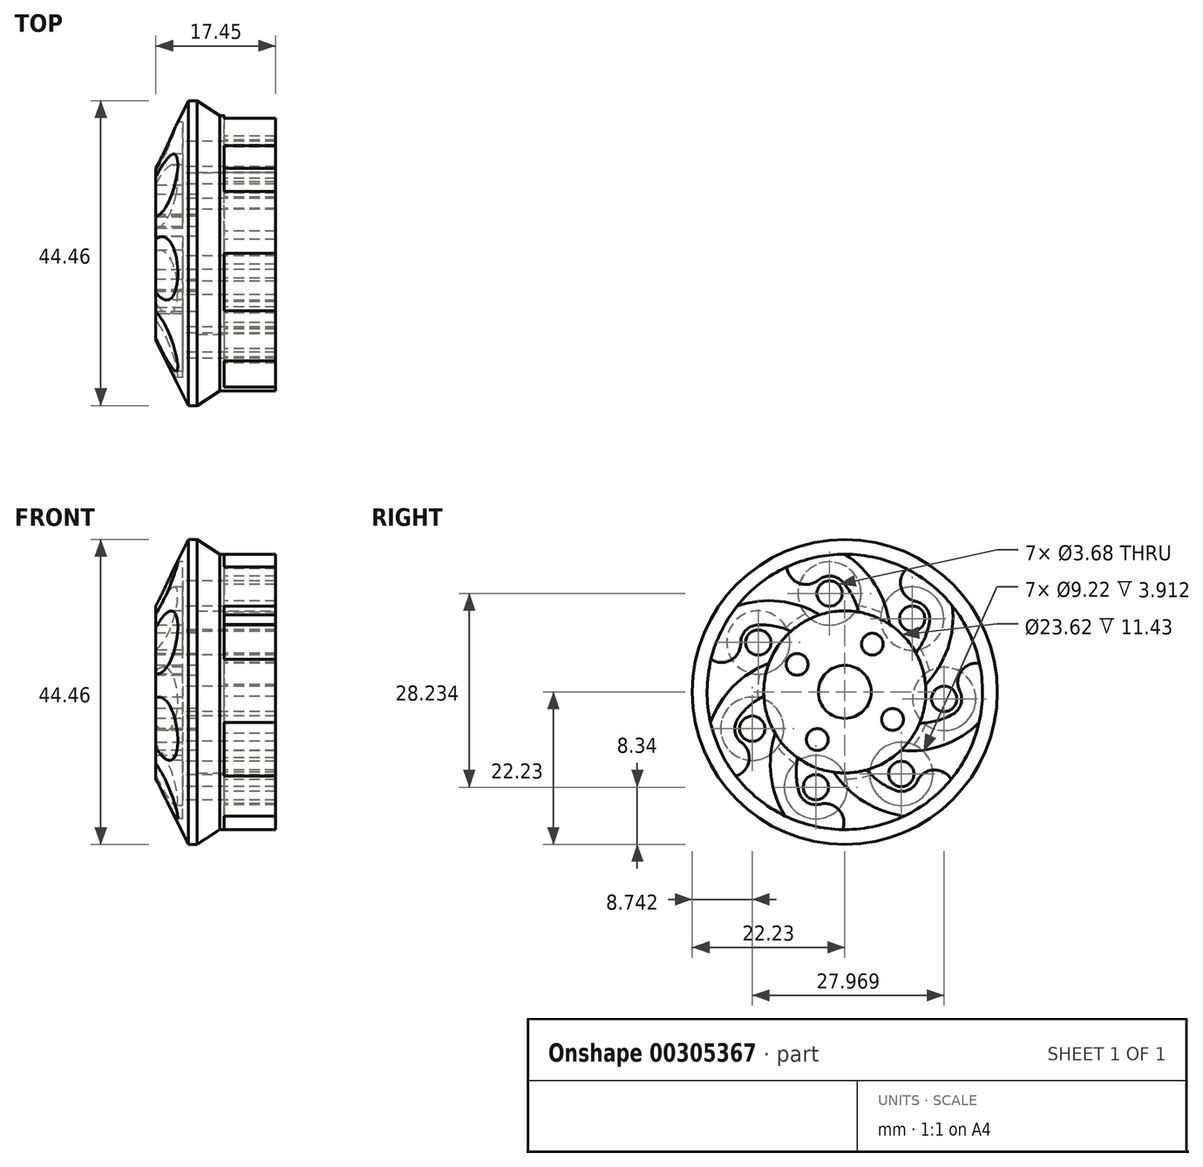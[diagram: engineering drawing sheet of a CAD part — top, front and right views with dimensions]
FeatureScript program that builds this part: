
annotation { "Feature Type Name" : "Feature", "Feature Type Description" : "" }
export const myFeature = defineFeature(function(context is Context, id is Id, definition is map)
    precondition{}
    {
        {
            var Q0;
            Q0=qCreatedBy(makeId("Top.planeOp"),FACE);
            var sketch = newSketch(context, id + "F0", { "sketchPlane" : qUnion([Q0])});
            skLineSegment(sketch, "E0", {"start": v(17.45, 0) * mm, "end": v(17.45, -12.7) * mm});
            skLineSegment(sketch, "E1", {"start": v(17.45, -12.7) * mm, "end": v(12.7, -22.23) * mm});
            skLineSegment(sketch, "E2", {"start": v(12.7, -22.23) * mm, "end": v(11.43, -22.23) * mm});
            skLineSegment(sketch, "E3", {"start": v(11.43, -22.23) * mm, "end": v(8.13, -20.07) * mm});
            skLineSegment(sketch, "E4", {"start": v(8.13, -20.07) * mm, "end": v(0, -20.07) * mm});
            skLineSegment(sketch, "E5", {"start": v(0, -20.07) * mm, "end": v(0, -11.81) * mm});
            skLineSegment(sketch, "E6", {"start": v(0, -11.81) * mm, "end": v(11.43, -11.81) * mm});
            skLineSegment(sketch, "E7", {"start": v(11.43, -11.81) * mm, "end": v(11.43, 0) * mm});
            skLineSegment(sketch, "E8", {"start": v(11.43, 0) * mm, "end": v(17.45, 0) * mm});
            skLineSegment(sketch, "E9", {"start": v(40.63, 0) * mm, "end": v(0, 0) * mm, "construction": true});
            skSolve(sketch);
        }
        {
            var Q0;
            Q0=qSketchRegion(id+"F0",true);
            var Q1;
            Q1=sQuery(id+"F0.wireOp",EDGE,"E9");
            revolve(context, id + "F1", {"entities" : qUnion([Q0]), "axis" : qUnion([Q1]), "revolveType" : RevolveType.FULL});
        }
        {
            var Q0;
            Q0=qCreatedBy(makeId("Right.planeOp"),FACE);
            var sketch = newSketch(context, id + "F2", { "sketchPlane" : qUnion([Q0])});
            skCircle(sketch, "E10.cCircle", {"center": v(0, 0) * mm, "radius": 20.07 * mm, "construction": true});
            skLineSegment(sketch, "E10.0", {"start": v(-9.66, 20.07) * mm, "end": v(9.66, 20.07) * mm, "construction": true});
            skLineSegment(sketch, "E10.1", {"start": v(9.66, 20.07) * mm, "end": v(21.71, 4.96) * mm, "construction": true});
            skLineSegment(sketch, "E10.2", {"start": v(21.71, 4.96) * mm, "end": v(17.41, -13.89) * mm, "construction": true});
            skLineSegment(sketch, "E10.3", {"start": v(17.41, -13.89) * mm, "end": v(0, -22.27) * mm, "construction": true});
            skLineSegment(sketch, "E10.4", {"start": v(0, -22.27) * mm, "end": v(-17.41, -13.89) * mm, "construction": true});
            skLineSegment(sketch, "E10.5", {"start": v(-17.41, -13.89) * mm, "end": v(-21.71, 4.96) * mm, "construction": true});
            skLineSegment(sketch, "E10.6", {"start": v(-21.71, 4.96) * mm, "end": v(-9.66, 20.07) * mm, "construction": true});
            skPoint(sketch, "E10.0.midPoint", {"position": v(0, 20.07) * mm});
            skLineSegment(sketch, "E11", {"start": v(0, 0) * mm, "end": v(0, 20.07) * mm, "construction": true});
            skLineSegment(sketch, "E12", {"start": v(0, 0) * mm, "end": v(-8.43, 18.2) * mm, "construction": true});
            skLineSegment(sketch, "E13", {"start": v(0, 0) * mm, "end": v(2.02, 11.64) * mm, "construction": true});
            skCircle(sketch, "E14", {"center": v(0, 0) * mm, "radius": 11.81 * mm, "construction": true});
            skPoint(sketch, "E15", {"position": v(0, 11.81) * mm});
            skLineSegment(sketch, "E16", {"start": v(0, 0) * mm, "end": v(6.5, 9.86) * mm, "construction": true});
            skArc(sketch, "E17", {"start": v(6.5, 9.86) * mm, "mid": v(4.4, 15.68) * mm, "end": v(0, 20.07) * mm});
            skCircle(sketch, "E18", {"center": v(0, 0) * mm, "radius": 14.52 * mm, "construction": true});
            skLineSegment(sketch, "E19", {"start": v(0, 0) * mm, "end": v(-2.23, 14.34) * mm, "construction": true});
            skPoint(sketch, "E20", {"position": v(0, 14.52) * mm});
            skCircle(sketch, "E21", {"center": v(-2.23, 14.34) * mm, "radius": 1.84 * mm, "construction": true});
            skArc(sketch, "E22", {"start": v(-0.35, 16.07) * mm, "mid": v(-2.06, 16.9) * mm, "end": v(-3.86, 16.3) * mm});
            skArc(sketch, "E23", {"start": v(2.02, 11.64) * mm, "mid": v(1.12, 14) * mm, "end": v(-0.35, 16.07) * mm});
            skArc(sketch, "E24", {"start": v(-8.43, 18.2) * mm, "mid": v(-6.72, 15.87) * mm, "end": v(-3.86, 16.3) * mm});
            skArc(sketch, "E25", {"start": v(0, 20.07) * mm, "mid": v(-4.73, 21.48) * mm, "end": v(-8.43, 18.2) * mm});
            skArc(sketch, "E26", {"start": v(2.02, 11.64) * mm, "mid": v(4.04, 10.18) * mm, "end": v(6.5, 9.86) * mm});
            skCircle(sketch, "E27", {"center": v(-2.23, 14.34) * mm, "radius": 1.84 * mm});
            skArc(sketch, "E28.1.0", {"start": v(-3.65, 11.23) * mm, "mid": v(-9.53, 13.21) * mm, "end": v(-15.69, 12.51) * mm});
            skArc(sketch, "E28.1.1", {"start": v(-7.84, 8.84) * mm, "mid": v(-5.44, 9.5) * mm, "end": v(-3.65, 11.23) * mm});
            skArc(sketch, "E28.1.2", {"start": v(-7.84, 8.84) * mm, "mid": v(-10.25, 9.6) * mm, "end": v(-12.78, 9.75) * mm});
            skArc(sketch, "E28.1.3", {"start": v(-12.78, 9.75) * mm, "mid": v(-14.49, 8.92) * mm, "end": v(-15.16, 7.15) * mm});
            skArc(sketch, "E28.1.4", {"start": v(-15.69, 12.51) * mm, "mid": v(-19.75, 9.7) * mm, "end": v(-19.5, 4.76) * mm});
            skArc(sketch, "E28.1.5", {"start": v(-19.5, 4.76) * mm, "mid": v(-16.6, 4.64) * mm, "end": v(-15.16, 7.15) * mm});
            skCircle(sketch, "E28.1.6", {"center": v(-12.6, 7.2) * mm, "radius": 1.84 * mm, "construction": true});
            skCircle(sketch, "E28.1.7", {"center": v(-12.6, 7.2) * mm, "radius": 1.84 * mm});
            skArc(sketch, "E28.2.0", {"start": v(-11.06, 4.15) * mm, "mid": v(-16.27, 0.8) * mm, "end": v(-19.56, -4.47) * mm});
            skArc(sketch, "E28.2.1", {"start": v(-11.8, -0.62) * mm, "mid": v(-10.82, 1.68) * mm, "end": v(-11.06, 4.15) * mm});
            skArc(sketch, "E28.2.2", {"start": v(-11.8, -0.62) * mm, "mid": v(-13.9, -2.03) * mm, "end": v(-15.59, -3.91) * mm});
            skArc(sketch, "E28.2.3", {"start": v(-15.59, -3.91) * mm, "mid": v(-16, -5.76) * mm, "end": v(-15.04, -7.4) * mm});
            skArc(sketch, "E28.2.4", {"start": v(-19.56, -4.47) * mm, "mid": v(-19.9, -9.4) * mm, "end": v(-15.87, -12.27) * mm});
            skArc(sketch, "E28.2.5", {"start": v(-15.87, -12.27) * mm, "mid": v(-13.98, -10.09) * mm, "end": v(-15.04, -7.4) * mm});
            skCircle(sketch, "E28.2.6", {"center": v(-13.49, -5.36) * mm, "radius": 1.84 * mm, "construction": true});
            skCircle(sketch, "E28.2.7", {"center": v(-13.49, -5.36) * mm, "radius": 1.84 * mm});
            skArc(sketch, "E28.3.0", {"start": v(-10.14, -6.05) * mm, "mid": v(-10.76, -12.23) * mm, "end": v(-8.7, -18.08) * mm});
            skArc(sketch, "E28.3.1", {"start": v(-6.87, -9.6) * mm, "mid": v(-8.06, -7.42) * mm, "end": v(-10.14, -6.05) * mm});
            skArc(sketch, "E28.3.2", {"start": v(-6.87, -9.6) * mm, "mid": v(-7.08, -12.13) * mm, "end": v(-6.66, -14.63) * mm});
            skArc(sketch, "E28.3.3", {"start": v(-6.66, -14.63) * mm, "mid": v(-5.48, -16.11) * mm, "end": v(-3.6, -16.37) * mm});
            skArc(sketch, "E28.3.4", {"start": v(-8.7, -18.08) * mm, "mid": v(-5.06, -21.41) * mm, "end": v(-0.3, -20.06) * mm});
            skArc(sketch, "E28.3.5", {"start": v(-0.3, -20.06) * mm, "mid": v(-0.83, -17.22) * mm, "end": v(-3.6, -16.37) * mm});
            skCircle(sketch, "E28.3.6", {"center": v(-4.22, -13.9) * mm, "radius": 1.84 * mm, "construction": true});
            skCircle(sketch, "E28.3.7", {"center": v(-4.22, -13.9) * mm, "radius": 1.84 * mm});
            skArc(sketch, "E28.4.0", {"start": v(-1.59, -11.7) * mm, "mid": v(2.85, -16.04) * mm, "end": v(8.7, -18.08) * mm});
            skArc(sketch, "E28.4.1", {"start": v(3.22, -11.36) * mm, "mid": v(0.77, -10.92) * mm, "end": v(-1.59, -11.7) * mm});
            skArc(sketch, "E28.4.2", {"start": v(3.22, -11.36) * mm, "mid": v(5.07, -13.1) * mm, "end": v(7.28, -14.33) * mm});
            skArc(sketch, "E28.4.3", {"start": v(7.28, -14.33) * mm, "mid": v(9.18, -14.33) * mm, "end": v(10.55, -13.01) * mm});
            skArc(sketch, "E28.4.4", {"start": v(8.7, -18.08) * mm, "mid": v(13.59, -17.3) * mm, "end": v(15.5, -12.75) * mm});
            skArc(sketch, "E28.4.5", {"start": v(15.5, -12.75) * mm, "mid": v(12.94, -11.38) * mm, "end": v(10.55, -13.01) * mm});
            skCircle(sketch, "E28.4.6", {"center": v(8.23, -11.96) * mm, "radius": 1.84 * mm, "construction": true});
            skCircle(sketch, "E28.4.7", {"center": v(8.23, -11.96) * mm, "radius": 1.84 * mm});
            skArc(sketch, "E28.5.0", {"start": v(8.16, -8.54) * mm, "mid": v(14.31, -7.77) * mm, "end": v(19.56, -4.47) * mm});
            skArc(sketch, "E28.5.1", {"start": v(10.9, -4.56) * mm, "mid": v(9.02, -6.2) * mm, "end": v(8.16, -8.54) * mm});
            skArc(sketch, "E28.5.2", {"start": v(10.9, -4.56) * mm, "mid": v(13.4, -4.2) * mm, "end": v(15.74, -3.24) * mm});
            skArc(sketch, "E28.5.3", {"start": v(15.74, -3.24) * mm, "mid": v(16.92, -1.75) * mm, "end": v(16.76, 0.14) * mm});
            skArc(sketch, "E28.5.4", {"start": v(19.56, -4.47) * mm, "mid": v(22, -0.17) * mm, "end": v(19.63, 4.17) * mm});
            skArc(sketch, "E28.5.5", {"start": v(19.63, 4.17) * mm, "mid": v(16.97, 3.02) * mm, "end": v(16.76, 0.14) * mm});
            skCircle(sketch, "E28.5.6", {"center": v(14.48, -1.02) * mm, "radius": 1.84 * mm, "construction": true});
            skCircle(sketch, "E28.5.7", {"center": v(14.48, -1.02) * mm, "radius": 1.84 * mm});
            skArc(sketch, "E28.6.0", {"start": v(11.76, 1.06) * mm, "mid": v(15, 6.35) * mm, "end": v(15.69, 12.51) * mm});
            skArc(sketch, "E28.6.1", {"start": v(10.36, 5.67) * mm, "mid": v(10.48, 3.19) * mm, "end": v(11.76, 1.06) * mm});
            skArc(sketch, "E28.6.2", {"start": v(10.36, 5.67) * mm, "mid": v(11.64, 7.86) * mm, "end": v(12.35, 10.29) * mm});
            skArc(sketch, "E28.6.3", {"start": v(12.35, 10.29) * mm, "mid": v(11.92, 12.14) * mm, "end": v(10.34, 13.19) * mm});
            skArc(sketch, "E28.6.4", {"start": v(15.69, 12.51) * mm, "mid": v(13.85, 17.1) * mm, "end": v(8.98, 17.95) * mm});
            skArc(sketch, "E28.6.5", {"start": v(8.98, 17.95) * mm, "mid": v(8.22, 15.15) * mm, "end": v(10.34, 13.19) * mm});
            skCircle(sketch, "E28.6.6", {"center": v(9.83, 10.69) * mm, "radius": 1.84 * mm, "construction": true});
            skCircle(sketch, "E28.6.7", {"center": v(9.83, 10.69) * mm, "radius": 1.84 * mm});
            skSolve(sketch);
        }
        {
            var Q0;
            Q0=qSketchRegion(id+"F2",true);
            extrude(context, id + "F3", {"entities" : qUnion([Q0]), "operationType" : NewBodyOperationType.REMOVE, "depth" : 7.52 * mm});
        }
        {
            var Q0;
            Q0=qCreatedBy(makeId("Right.planeOp"),FACE);
            var sketch = newSketch(context, id + "F4", { "sketchPlane" : qUnion([Q0])});
            skCircle(sketch, "E29", {"center": v(9.83, 10.69) * mm, "radius": 1.84 * mm});
            skCircle(sketch, "E30.1.0", {"center": v(-2.23, 14.34) * mm, "radius": 1.84 * mm});
            skCircle(sketch, "E30.2.0", {"center": v(-12.6, 7.2) * mm, "radius": 1.84 * mm});
            skCircle(sketch, "E30.3.0", {"center": v(-13.49, -5.36) * mm, "radius": 1.84 * mm});
            skCircle(sketch, "E30.4.0", {"center": v(-4.22, -13.9) * mm, "radius": 1.84 * mm});
            skCircle(sketch, "E30.5.0", {"center": v(8.23, -11.96) * mm, "radius": 1.84 * mm});
            skCircle(sketch, "E30.6.0", {"center": v(14.48, -1.02) * mm, "radius": 1.84 * mm});
            skPoint(sketch, "E30.center", {"position": v(0, 0) * mm});
            skSolve(sketch);
        }
        {
            var Q0;
            Q0=makeQuery(id+"F4.imprint","IMPRINT",FACE,{"disambiguationData":[TD([[makeQuery(id+"F4.imprint","IMPRINT",EDGE,{"derivedFrom":sQuery(id+"F4.wireOp",EDGE,"E29")}),1.0]])]});
            var Q1;
            Q1=makeQuery(id+"F4.imprint","IMPRINT",FACE,{"disambiguationData":[TD([[makeQuery(id+"F4.imprint","IMPRINT",EDGE,{"derivedFrom":sQuery(id+"F4.wireOp",EDGE,"E30.1.0")}),1.0]])]});
            var Q2;
            Q2=makeQuery(id+"F4.imprint","IMPRINT",FACE,{"disambiguationData":[TD([[makeQuery(id+"F4.imprint","IMPRINT",EDGE,{"derivedFrom":sQuery(id+"F4.wireOp",EDGE,"E30.2.0")}),1.0]])]});
            var Q3;
            Q3=makeQuery(id+"F4.imprint","IMPRINT",FACE,{"disambiguationData":[TD([[makeQuery(id+"F4.imprint","IMPRINT",EDGE,{"derivedFrom":sQuery(id+"F4.wireOp",EDGE,"E30.3.0")}),1.0]])]});
            var Q4;
            Q4=makeQuery(id+"F4.imprint","IMPRINT",FACE,{"disambiguationData":[TD([[makeQuery(id+"F4.imprint","IMPRINT",EDGE,{"derivedFrom":sQuery(id+"F4.wireOp",EDGE,"E30.4.0")}),1.0]])]});
            var Q5;
            Q5=makeQuery(id+"F4.imprint","IMPRINT",FACE,{"disambiguationData":[TD([[makeQuery(id+"F4.imprint","IMPRINT",EDGE,{"derivedFrom":sQuery(id+"F4.wireOp",EDGE,"E30.5.0")}),1.0]])]});
            var Q6;
            Q6=makeQuery(id+"F4.imprint","IMPRINT",FACE,{"disambiguationData":[TD([[makeQuery(id+"F4.imprint","IMPRINT",EDGE,{"derivedFrom":sQuery(id+"F4.wireOp",EDGE,"E30.6.0")}),1.0]])]});
            extrude(context, id + "F5", {"entities" : qUnion([Q0, Q1, Q2, Q3, Q4, Q5, Q6]), "operationType" : NewBodyOperationType.REMOVE, "endBound" : BoundingType.THROUGH_ALL, "depth" : 25.4 * mm});
        }
        {
            var Q0;
            Q0=qCreatedBy(makeId("Right.planeOp"),FACE);
            cPlane(context, id + "F6", {"entities" : qUnion([Q0]), "cplaneType" : CPlaneType.OFFSET, "offset" : 17.45 * mm, "width" : 152.4 * mm, "height" : 152.4 * mm});
        }
        {
            var Q0;
            Q0=qCreatedBy(id+"F6.planeOp",FACE);
            var sketch = newSketch(context, id + "F7", { "sketchPlane" : qUnion([Q0])});
            skCircle(sketch, "E31", {"center": v(14.48, -1.02) * mm, "radius": 4.61 * mm});
            skCircle(sketch, "E32.1.0", {"center": v(9.83, 10.69) * mm, "radius": 4.61 * mm});
            skCircle(sketch, "E32.2.0", {"center": v(-2.23, 14.34) * mm, "radius": 4.61 * mm});
            skCircle(sketch, "E32.3.0", {"center": v(-12.6, 7.2) * mm, "radius": 4.61 * mm});
            skCircle(sketch, "E32.4.0", {"center": v(-13.49, -5.36) * mm, "radius": 4.61 * mm});
            skCircle(sketch, "E32.5.0", {"center": v(-4.22, -13.9) * mm, "radius": 4.61 * mm});
            skCircle(sketch, "E32.6.0", {"center": v(8.23, -11.96) * mm, "radius": 4.61 * mm});
            skPoint(sketch, "E32.center", {"position": v(0, 0) * mm});
            skSolve(sketch);
        }
        {
            var Q0;
            Q0=qSketchRegion(id+"F7",true);
            extrude(context, id + "F8", {"entities" : qUnion([Q0]), "operationType" : NewBodyOperationType.REMOVE, "oppositeDirection" : true, "depth" : 3.91 * mm});
        }
        {
            var Q0;
            Q0=qCreatedBy(id+"F6.planeOp",FACE);
            var sketch = newSketch(context, id + "F9", { "sketchPlane" : qUnion([Q0])});
            skCircle(sketch, "E33", {"center": v(0, 0) * mm, "radius": 3.86 * mm});
            skCircle(sketch, "E34", {"center": v(6.95, -4.01) * mm, "radius": 1.59 * mm});
            skLineSegment(sketch, "E35", {"start": v(0, 0) * mm, "end": v(22.23, 0) * mm, "construction": true});
            skLineSegment(sketch, "E36", {"start": v(0, 0) * mm, "end": v(6.95, -4.01) * mm, "construction": true});
            skCircle(sketch, "E37.1.0", {"center": v(4.01, 6.95) * mm, "radius": 1.59 * mm});
            skCircle(sketch, "E37.2.0", {"center": v(-6.95, 4.01) * mm, "radius": 1.59 * mm});
            skCircle(sketch, "E37.3.0", {"center": v(-4.01, -6.95) * mm, "radius": 1.59 * mm});
            skSolve(sketch);
        }
        {
            var Q0;
            Q0=qSketchRegion(id+"F9",true);
            extrude(context, id + "F10", {"entities" : qUnion([Q0]), "operationType" : NewBodyOperationType.REMOVE, "endBound" : BoundingType.THROUGH_ALL, "oppositeDirection" : true, "depth" : 25.4 * mm});
        }
        {
            var Q0;
            Q0=makeQuery(id+"F1.opRevolve","SWEPT_BODY",BODY,{"disambiguationData":[OSD([sQuery(id+"F0.wireOp",EDGE,"E0"),sQuery(id+"F0.wireOp",EDGE,"E1"),sQuery(id+"F0.wireOp",EDGE,"E2"),sQuery(id+"F0.wireOp",EDGE,"E3"),sQuery(id+"F0.wireOp",EDGE,"E4"),sQuery(id+"F0.wireOp",EDGE,"E5"),sQuery(id+"F0.wireOp",EDGE,"E6"),sQuery(id+"F0.wireOp",EDGE,"E7"),sQuery(id+"F0.wireOp",EDGE,"E8")])]});
            var Q1;
            Q1=qCreatedBy(makeId("Right.planeOp"),FACE);
            mirror(context, id + "F11", {"operationType" : NewBodyOperationType.ADD, "entities" : qUnion([Q0]), "mirrorPlane" : qUnion([Q1])});
        }
        {
            var Q0;
            Q0=qCreatedBy(makeId("Front.planeOp"),FACE);
            var sketch = newSketch(context, id + "F12", { "sketchPlane" : qUnion([Q0])});
            skLineSegment(sketch, "E38.bottom", {"start": v(38.1, 38.1) * mm, "end": v(0, 38.1) * mm});
            skLineSegment(sketch, "E38.top", {"start": v(38.1, -38.1) * mm, "end": v(0, -38.1) * mm});
            skLineSegment(sketch, "E38.left", {"start": v(38.1, 38.1) * mm, "end": v(38.1, -38.1) * mm});
            skLineSegment(sketch, "E38.right", {"start": v(0, 38.1) * mm, "end": v(0, -38.1) * mm});
            skSolve(sketch);
        }
        {
            var Q0;
            Q0 = qSketchRegion(id + "F12", true);
            extrude(context, id + "F13", {"entities" : qUnion([Q0]), "operationType" : NewBodyOperationType.REMOVE, "endBound" : BoundingType.SYMMETRIC, "oppositeDirection" : true, "depth" : 76.2 * mm});
        }
    });
